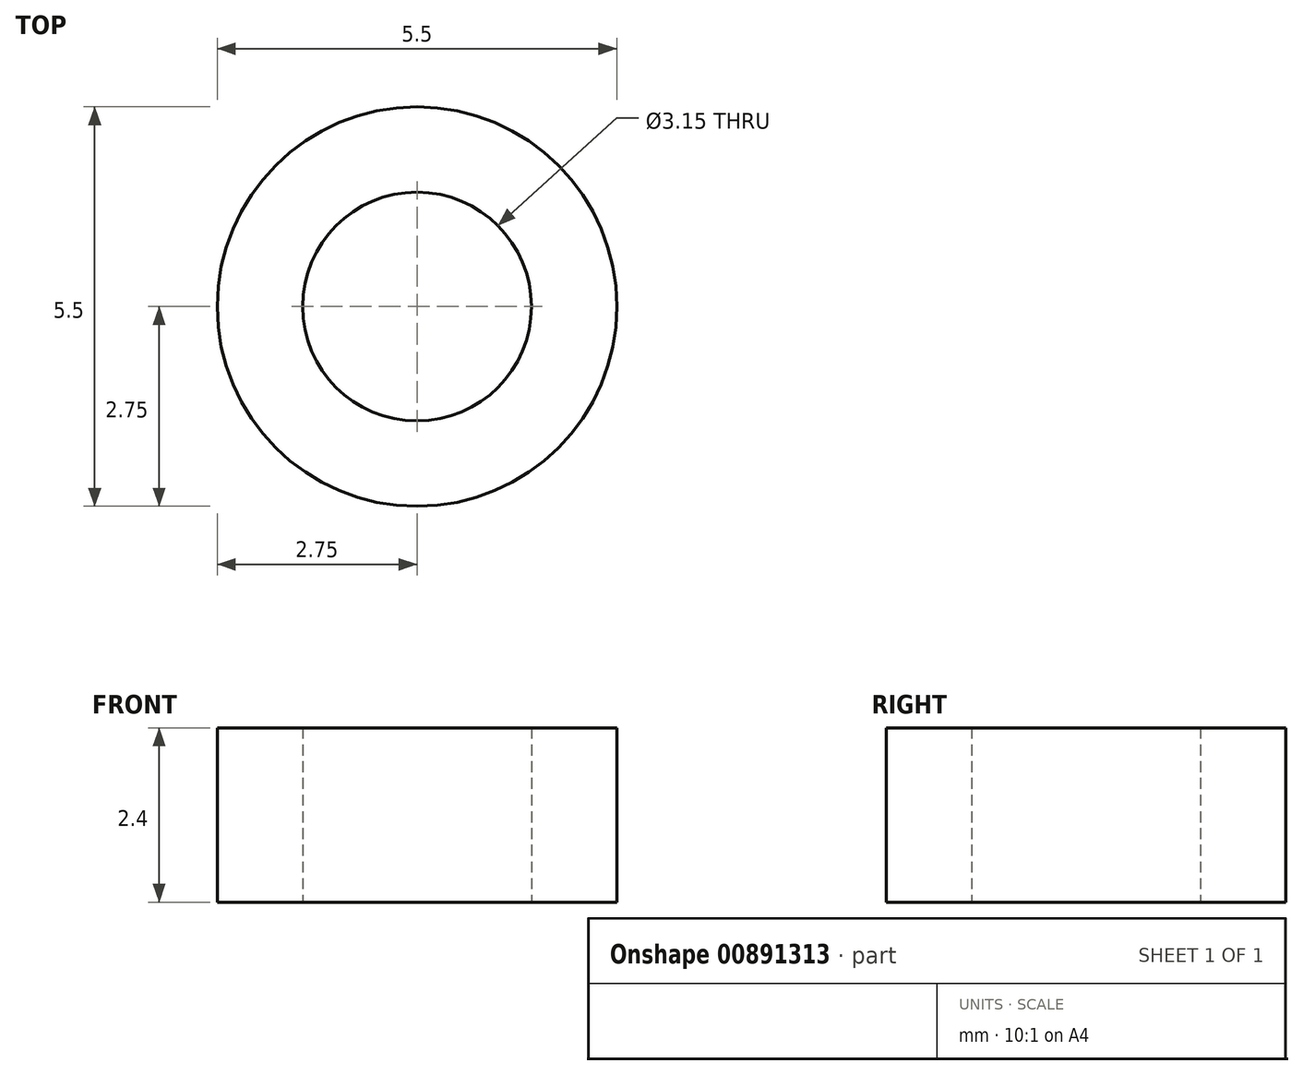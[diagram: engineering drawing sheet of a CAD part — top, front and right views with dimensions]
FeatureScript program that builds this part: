
annotation { "Feature Type Name" : "Feature", "Feature Type Description" : "" }
export const myFeature = defineFeature(function(context is Context, id is Id, definition is map)
    precondition{}
    {
        {
            var Q0;
            Q0=qCreatedBy(makeId("Top.planeOp"),FACE);
            var sketch = newSketch(context, id + "F0", { "sketchPlane" : qUnion([Q0])});
            skCircle(sketch, "E0", {"center": v(0, 0) * mm, "radius": 1.58 * mm});
            skCircle(sketch, "E1", {"center": v(0, 0) * mm, "radius": 2.75 * mm});
            skSolve(sketch);
        }
        {
            var Q0;
            Q0=qSketchRegion(id+"F0",true);
            extrude(context, id + "F1", {"entities" : qUnion([Q0]), "depth" : 2.4 * mm, "offsetDistance" : 25 * mm});
        }
    });
